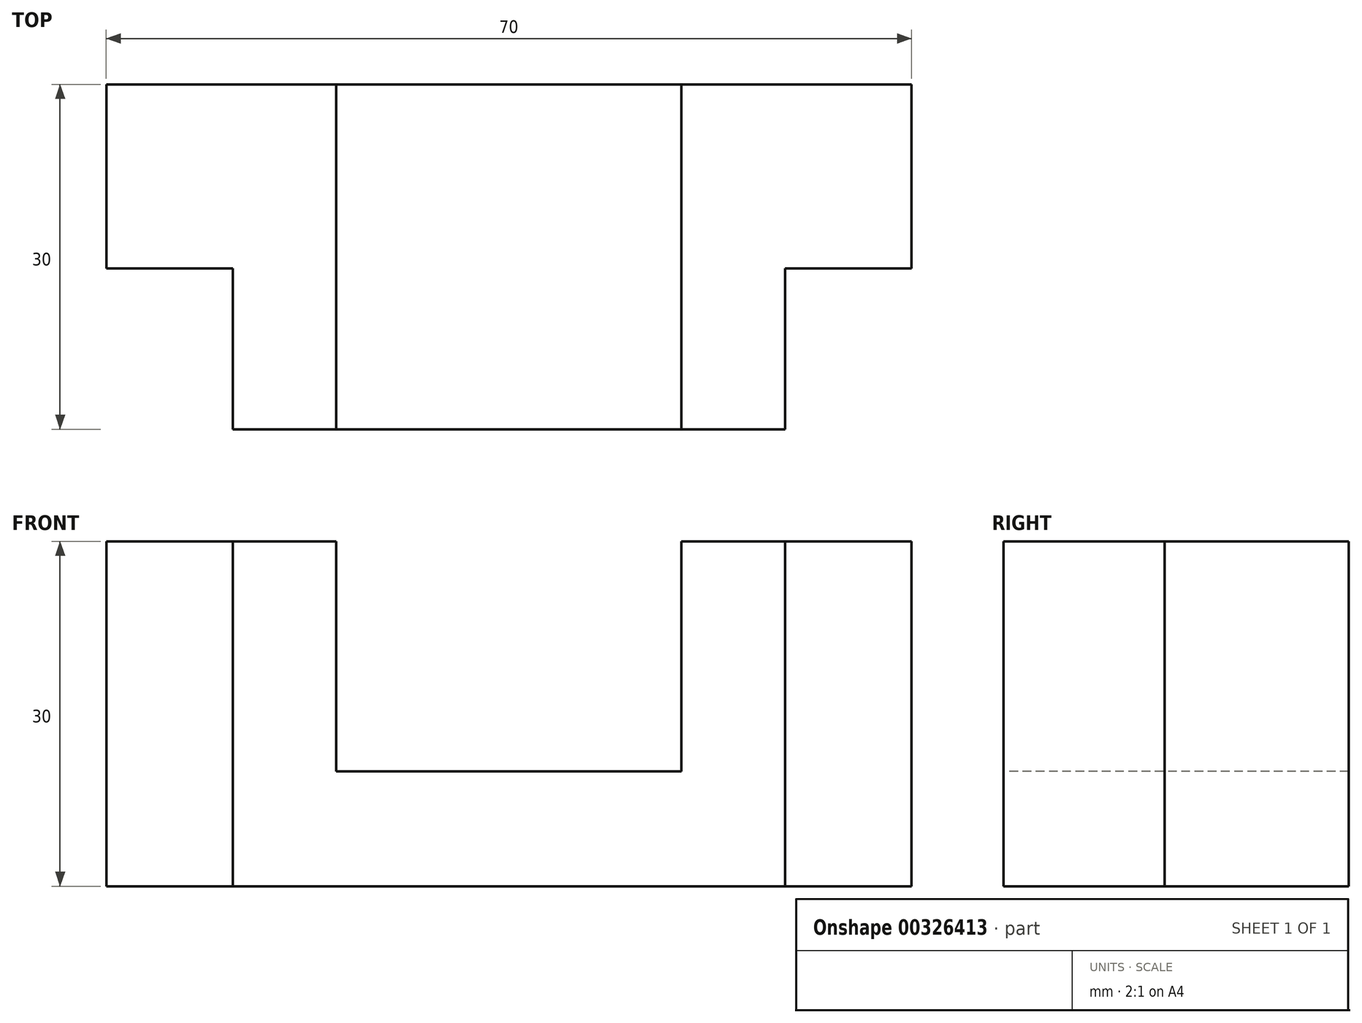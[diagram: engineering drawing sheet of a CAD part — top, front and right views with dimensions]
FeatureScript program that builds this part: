
annotation { "Feature Type Name" : "Feature", "Feature Type Description" : "" }
export const myFeature = defineFeature(function(context is Context, id is Id, definition is map)
    precondition{}
    {
        {
            var Q0;
            Q0=qCreatedBy(makeId("Top.planeOp"),FACE);
            var sketch = newSketch(context, id + "F0", { "sketchPlane" : qUnion([Q0])});
            skLineSegment(sketch, "E0", {"start": v(-45.54, -17.73) * mm, "end": v(24.46, -17.73) * mm});
            skLineSegment(sketch, "E1", {"start": v(24.46, -17.73) * mm, "end": v(24.46, -33.73) * mm});
            skLineSegment(sketch, "E2", {"start": v(24.46, -33.73) * mm, "end": v(13.46, -33.73) * mm});
            skLineSegment(sketch, "E3", {"start": v(13.46, -33.73) * mm, "end": v(13.46, -47.73) * mm});
            skLineSegment(sketch, "E4", {"start": v(13.46, -47.73) * mm, "end": v(-34.54, -47.73) * mm});
            skLineSegment(sketch, "E5", {"start": v(-34.54, -47.73) * mm, "end": v(-34.54, -33.73) * mm});
            skLineSegment(sketch, "E6", {"start": v(-34.54, -33.73) * mm, "end": v(-45.54, -33.73) * mm});
            skLineSegment(sketch, "E7", {"start": v(-45.54, -33.73) * mm, "end": v(-45.54, -17.73) * mm});
            skLineSegment(sketch, "E8", {"start": v(-25.54, -17.73) * mm, "end": v(-25.54, -47.73) * mm});
            skLineSegment(sketch, "E9", {"start": v(4.46, -17.73) * mm, "end": v(4.46, -47.73) * mm});
            skSolve(sketch);
        }
        {
            var Q0;
            {var subQ0=sQuery(id+"F0.wireOp",EDGE,"E8");Q0=makeQuery(id+"F0.imprint","IMPRINT",FACE,{"disambiguationData":[TD([[makeQuery(id+"F0.imprint","IMPRINT",EDGE,{"derivedFrom":subQ0}),1.0]])]});}
            extrude(context, id + "F1", {"entities" : qUnion([Q0]), "depth" : 10 * mm});
        }
        {
            var Q0;
            {var subQ0=sQuery(id+"F0.wireOp",EDGE,"E5");Q0=makeQuery(id+"F0.imprint","IMPRINT",FACE,{"disambiguationData":[TD([[makeQuery(id+"F0.imprint","IMPRINT",EDGE,{"derivedFrom":subQ0}),-1.0]])]});}
            var Q1;
            {var subQ1=sQuery(id+"F0.wireOp",EDGE,"E1");Q1=makeQuery(id+"F0.imprint","IMPRINT",FACE,{"disambiguationData":[TD([[makeQuery(id+"F0.imprint","IMPRINT",EDGE,{"derivedFrom":subQ1}),-1.0]])]});}
            extrude(context, id + "F2", {"entities" : qUnion([Q0, Q1]), "operationType" : NewBodyOperationType.ADD, "depth" : 30 * mm});
        }
    });
